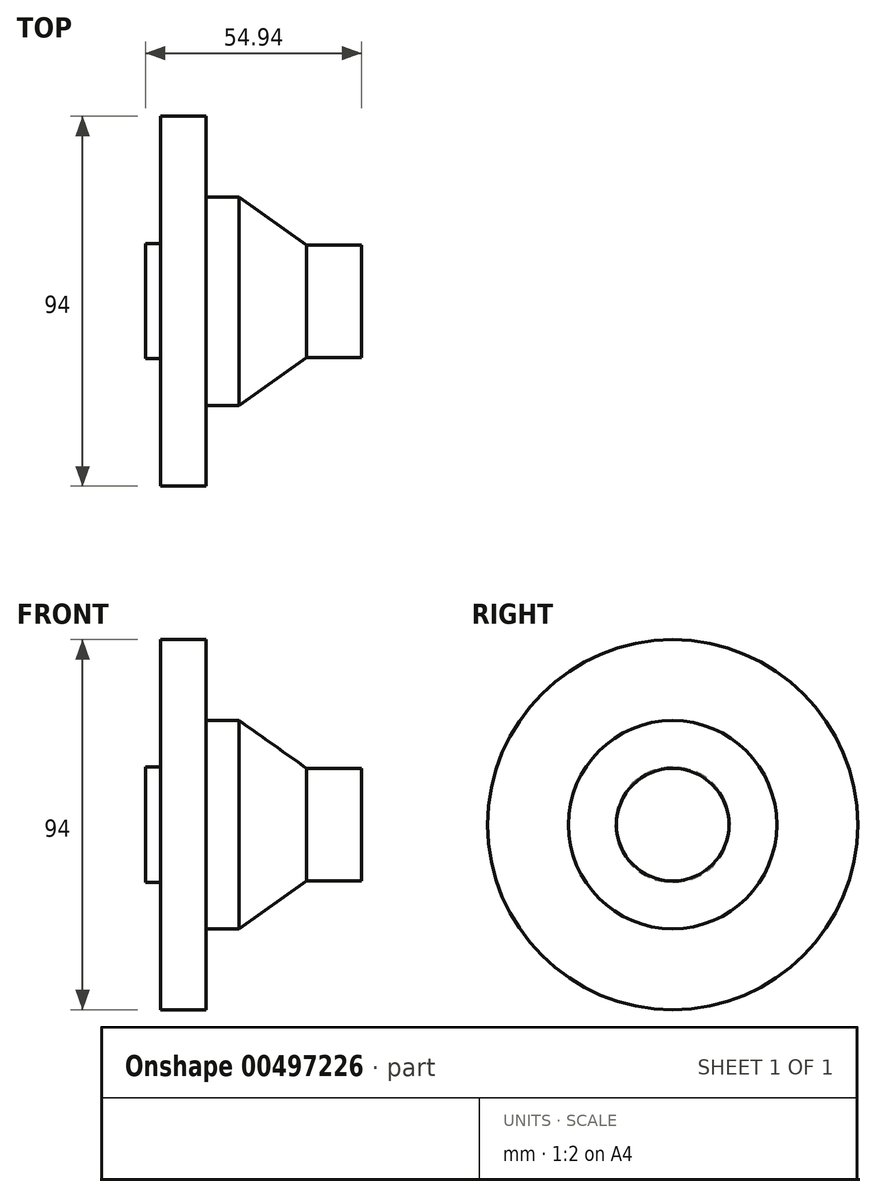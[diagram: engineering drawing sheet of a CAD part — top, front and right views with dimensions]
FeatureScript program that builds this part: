
annotation { "Feature Type Name" : "Feature", "Feature Type Description" : "" }
export const myFeature = defineFeature(function(context is Context, id is Id, definition is map)
    precondition{}
    {
        {
            var Q0;
            Q0=qCreatedBy(makeId("Front.planeOp"),FACE);
            var sketch = newSketch(context, id + "F0", { "sketchPlane" : qUnion([Q0])});
            skLineSegment(sketch, "E0", {"start": v(0, 0) * mm, "end": v(54.94, 0) * mm});
            skLineSegment(sketch, "E1", {"start": v(54.94, 14.32) * mm, "end": v(40.93, 14.32) * mm});
            skLineSegment(sketch, "E2", {"start": v(40.93, 14.32) * mm, "end": v(23.81, 26.46) * mm});
            skLineSegment(sketch, "E3", {"start": v(23.81, 26.46) * mm, "end": v(15.4, 26.46) * mm});
            skLineSegment(sketch, "E4", {"start": v(15.4, 26.46) * mm, "end": v(15.4, 47) * mm});
            skLineSegment(sketch, "E5", {"start": v(15.4, 47) * mm, "end": v(3.9, 47) * mm});
            skLineSegment(sketch, "E6", {"start": v(3.9, 47) * mm, "end": v(3.9, 14.63) * mm});
            skLineSegment(sketch, "E7", {"start": v(3.9, 14.63) * mm, "end": v(0, 14.63) * mm});
            skLineSegment(sketch, "E8", {"start": v(0, 14.63) * mm, "end": v(0, 0) * mm});
            skLineSegment(sketch, "E9", {"start": v(54.94, 14.32) * mm, "end": v(54.94, 0) * mm});
            skSolve(sketch);
        }
        {
            var Q0;
            Q0 = qSketchRegion(id + "F0", true);
            var Q1;
            Q1=sQuery(id+"F0.wireOp",EDGE,"E0");
            revolve(context, id + "F1", {"entities" : qUnion([Q0]), "axis" : qUnion([Q1]), "revolveType" : RevolveType.FULL});
        }
    });
